# Revit family: Sanext_Осевой сильфонный компенсатор
name_source: partatom
category: Арматура трубопроводов
revit_build: Autodesk Revit 2017 (Build: 20171027_0315(x64)
units: mm (PartAtom-declared; Revit-internal decimal feet)

## family parameters
Всегда вертикально = Да
На основе рабочей плоскости = Нет
Общий = Нет
При загрузке вырезать с полостями = Нет
Размер круглого соединителя = Использовать диаметр
Тип детали = Вставляется

## types (1)
- Sanext_Осевой сильфонный компенсатор
    ADSK_Единица измерения = шт
    ADSK_Завод-изготовитель = ООО САНЕКСТ.ПРО
    ADSK_Материал наименование = Алюминий
    URL = http://sanext.ru
    z = 0
    Группа модели = Осевой сильфонный компенсатор
    Изготовитель = ООО САНЕКСТ.ПРО
    Материал стальной части = Алюминий
    Описание = Компенсатор многослойный сильфон с кожухом под приварку Ру 16
    Рабочее давление = 0.0 кПа
    Разработчик = ООО ПРОРУБИМ
    Разработчик (телефон) = +7(495)649-85-43
    Разработчик модели (URL) = http://prorubim.com
